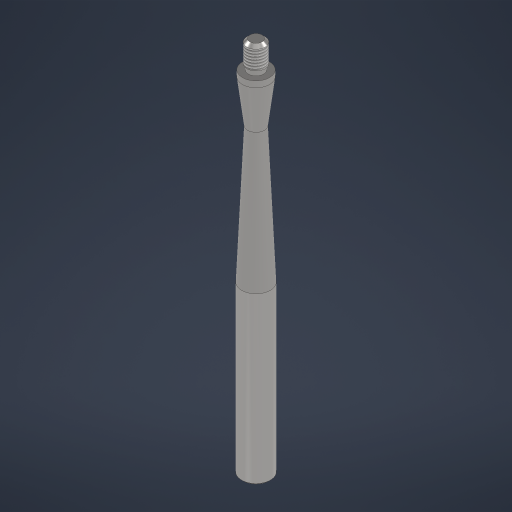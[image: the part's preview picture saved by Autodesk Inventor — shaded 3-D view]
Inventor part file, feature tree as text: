
AUTODESK INVENTOR PART (.ipt)
format: ipt  version: 2024.3 (Build 283343000, 343)  size: 229,888 bytes
history: native  units: mm
features: chamfer x2, sketch x2, revolve x1, thread x1, hole x1, other x1
ambient origin geometry x8: Origin, YZ Plane, XZ Plane, XY Plane, X Axis, Y Axis, Z Axis, Center Point
bodies: Solid1 (feature_tree)
feature tree (8):
  revolve  "Revolution1"  [1 undecoded]
  thread  "Thread1"  [1 undecoded]
  hole  "Hole1"  [1 undecoded]
  chamfer  "Chamfer2"  Distance=3.0mm
  chamfer  "Chamfer3"  Distance=18.0mm
  sketch  "Sketch1"  dims[d0=250.0mm d1=19.0mm d2=110.0mm]
  sketch  "Sketch2"  dims[d5=11.14103mm d6=12.0mm d7=3.0mm d9=18.0mm d10=4.0mm d11=10.0mm d12=60.0deg d13=18.0mm d14=0.436332mm d15=90.0deg d16=1.218746mm d17=200.0mm d18=232.0mm d19=50.0mm d20=14.42265mm d21=13.268mm d22=0.0mm d23=15.0mm d24=0.5mm d25=15.5mm d26=2.0mm d27=90.0deg d28=80.0mm d29=20.594885mm d41=2.0mm d42=2.0mm d43=45.0deg d44=1.0mm d45=2.0mm d46=45.0deg]
  other  "Finish1"
note: 3 required parameter values undecoded (feature->parameter linkage not recoverable at this tier; creation-order binding heuristic only, values carry confidence <= 0.55)